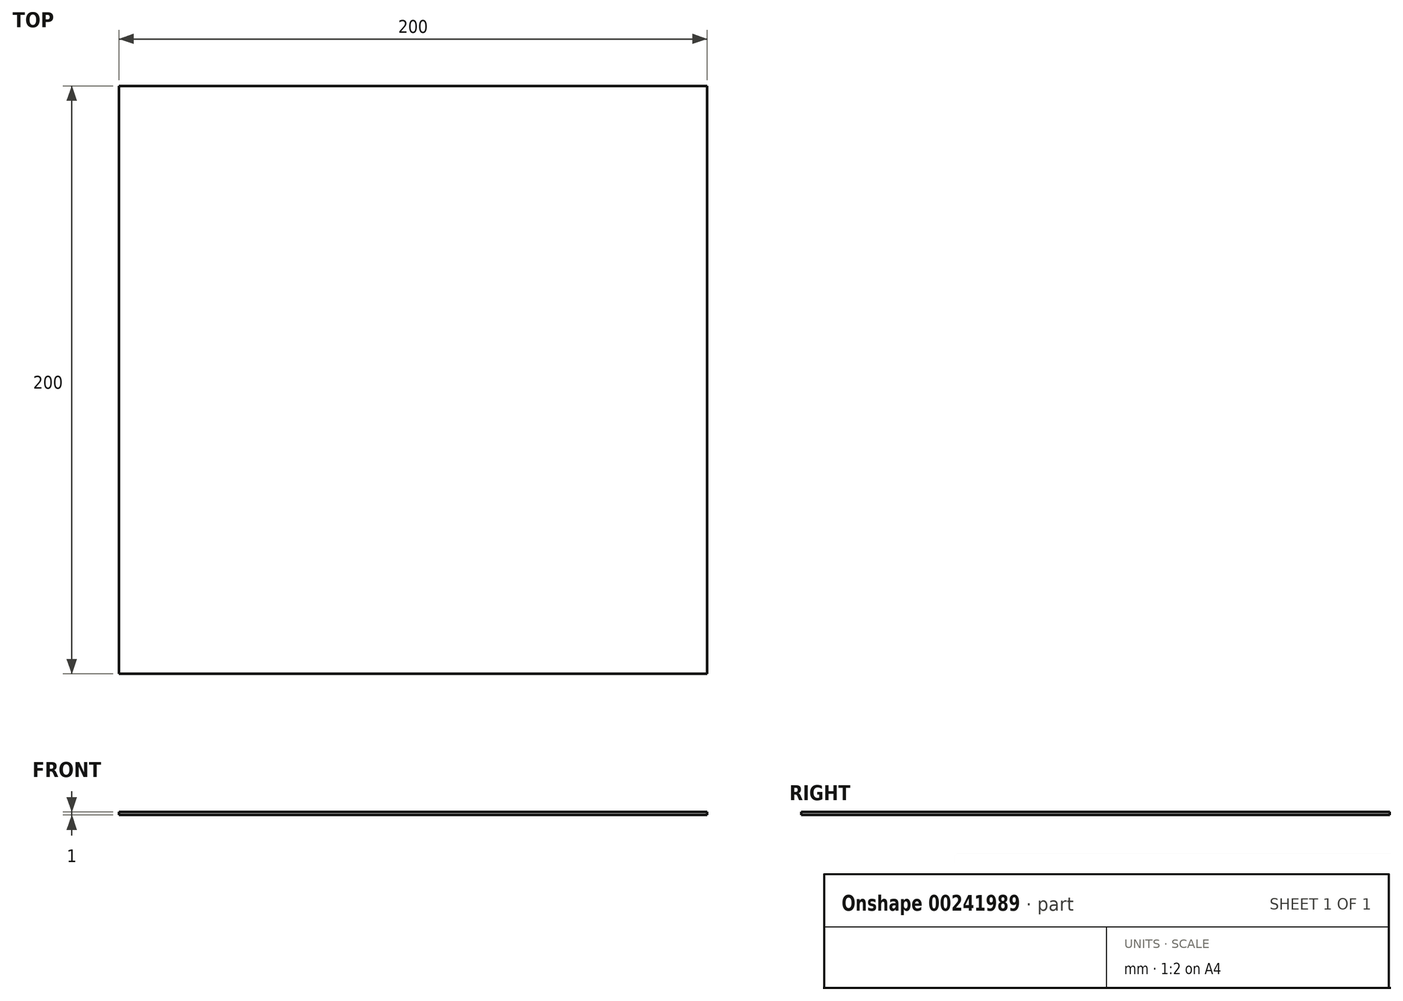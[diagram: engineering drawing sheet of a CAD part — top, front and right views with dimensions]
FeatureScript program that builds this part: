
annotation { "Feature Type Name" : "Feature", "Feature Type Description" : "" }
export const myFeature = defineFeature(function(context is Context, id is Id, definition is map)
    precondition{}
    {
        {
            var Q0;
            Q0=qCreatedBy(makeId("Top.planeOp"),FACE);
            var sketch = newSketch(context, id + "F0", { "sketchPlane" : qUnion([Q0])});
            skLineSegment(sketch, "E0.bottom", {"start": v(100, -100) * mm, "end": v(-100, -100) * mm});
            skLineSegment(sketch, "E0.top", {"start": v(100, 100) * mm, "end": v(-100, 100) * mm});
            skLineSegment(sketch, "E0.left", {"start": v(100, -100) * mm, "end": v(100, 100) * mm});
            skLineSegment(sketch, "E0.right", {"start": v(-100, -100) * mm, "end": v(-100, 100) * mm});
            skPoint(sketch, "E0.middle", {"position": v(0, 0) * mm});
            skSolve(sketch);
        }
        {
            var Q0;
            Q0 = qSketchRegion(id + "F0", true);
            extrude(context, id + "F1", {"entities" : qUnion([Q0]), "oppositeDirection" : true, "depth" : 1 * mm});
        }
    });
